# Revit family: NLRS_57_DUA_UN_round firedamper with smokesensor fdc25-ug_sacs
name_source: partatom
category: Duct Accessories
units: mm (PartAtom-declared; Revit-internal decimal feet)

## family parameters
Always vertical = Yes
Cut with Voids When Loaded = No
Part Type = Breaks Into
Round Connector Dimension = Use Diameter
Shared = No
Work Plane-Based = No

## types (12) — shared parameters
Article_Data = FDC25-UG_Article_Data
Assembly Code = 57.70
Blade material = Hittebestendig dikte 25mm
Casing material = Gegalvaniseerd plaatstaal
Description = Ronde brandklep met rooksensor
FireRating = EN 1366-2 and EN 13501-3, 2h
Fuse temperatuur (default) = 72 °C
IfcDescription = Ronde brandklep met rooksensor
IfcExportAs = IfcDamperType
IfcExportType = FIREDAMPER
LoadBearing = No
Manufacturer = Solid Air Climate Solutions
Model = Brandklep met rooksensor - Rond
NLRS_C_content_datum_uitgifte = 13-05-2021
NLRS_C_content_provider = Solid Air Climate Systems
NLRS_C_content_versie = Versie 3.19.01
NLRS_C_description = Ronde brandklep met rooksensor
NLRS_C_niveau ontwikkeling = LOD400
SACS_Cin_Offst = 42 mm  [stored 0.137795 ft]
SACS_Dummy = 1
SACS_Index3 = 1 mm  [stored 0.00328084 ft]
Selection_Factors = Selection_Factors
Show Symbol = Yes
Type Comments = Check airflow direction!
URL = https://solid-air.nl

## per-type parameters (varying)
| type | SACS_Index1 | SACS_Index2 | SACS_X_Offset |
| FDC25 O M24S UG | 0 mm  [stored 0 ft] | 3 mm  [stored 0.00984252 ft] | 220 mm  [stored 0.721785 ft] |
| FDC25 O M230S UG | 0 mm  [stored 0 ft] | 4 mm  [stored 0.0131234 ft] | 220 mm  [stored 0.721785 ft] |
| FDC25 APP M24S UG | 1 mm  [stored 0.00328084 ft] | 3 mm  [stored 0.00984252 ft] | 235 mm  [stored 0.770997 ft] |
| FDC25 APP M230S UG | 1 mm  [stored 0.00328084 ft] | 4 mm  [stored 0.0131234 ft] | 235 mm  [stored 0.770997 ft] |
| FDC25 APP EX UG | 1 mm  [stored 0.00328084 ft] | 6 mm  [stored 0.019685 ft] | 235 mm  [stored 0.770997 ft] |
| FDC25 MF1 M24S UG | 2 mm  [stored 0.00656168 ft] | 3 mm  [stored 0.00984252 ft] | 318 mm  [stored 1.04331 ft] |
| FDC25 MF1 M230S UG | 2 mm  [stored 0.00656168 ft] | 4 mm  [stored 0.0131234 ft] | 318 mm  [stored 1.04331 ft] |
| FDC25 MF1 EX UG | 2 mm  [stored 0.00656168 ft] | 6 mm  [stored 0.019685 ft] | 318 mm  [stored 1.04331 ft] |
| FDC25 MF2 M24S UG | 3 mm  [stored 0.00984252 ft] | 3 mm  [stored 0.00984252 ft] | 315 mm  [stored 1.03346 ft] |
| FDC25 MF2 M230S UG | 3 mm  [stored 0.00984252 ft] | 4 mm  [stored 0.0131234 ft] | 315 mm  [stored 1.03346 ft] |
| FDC25 MF2 EX UG | 3 mm  [stored 0.00984252 ft] | 6 mm  [stored 0.019685 ft] | 315 mm  [stored 1.03346 ft] |
| FDC25 O EX UG | 0 mm  [stored 0 ft] | 6 mm  [stored 0.019685 ft] | 220 mm  [stored 0.721785 ft] |

note: [stored X ft] marks values corroborated as IEEE doubles in the binary element streams (Revit-internal decimal feet)

## geometry (parser evidence)
native form markers: Sweep x33
no freeform markers — native parametric forms only
